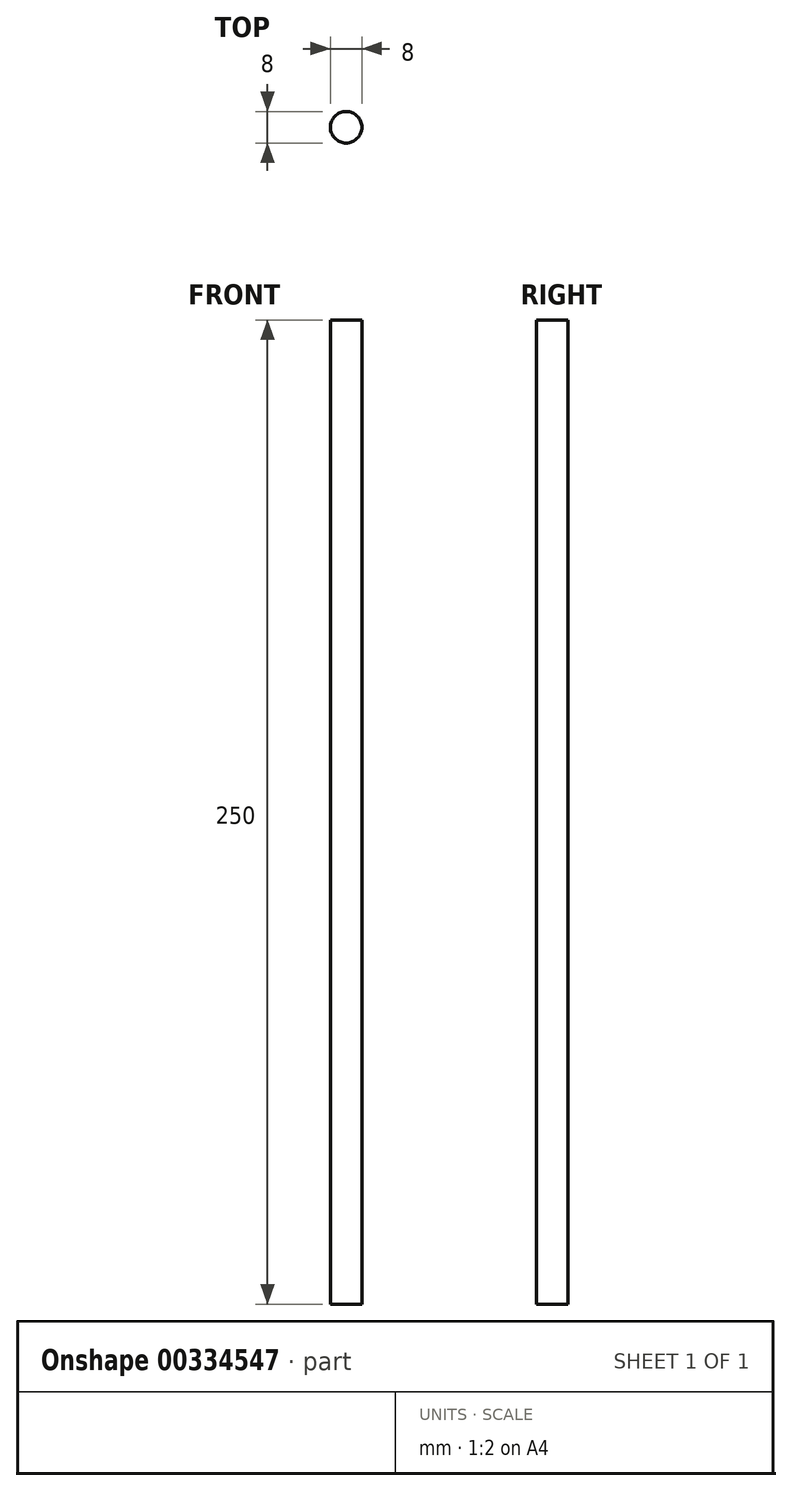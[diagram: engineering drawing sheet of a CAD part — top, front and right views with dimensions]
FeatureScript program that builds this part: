
annotation { "Feature Type Name" : "Feature", "Feature Type Description" : "" }
export const myFeature = defineFeature(function(context is Context, id is Id, definition is map)
    precondition{}
    {
        {
            var Q0;
            Q0=qCreatedBy(makeId("Top.planeOp"),FACE);
            var sketch = newSketch(context, id + "F0", { "sketchPlane" : qUnion([Q0])});
            skCircle(sketch, "E0", {"center": v(0, 0) * mm, "radius": 4 * mm});
            skSolve(sketch);
        }
        {
            var Q0;
            Q0 = qSketchRegion(id + "F0", true);
            extrude(context, id + "F1", {"entities" : qUnion([Q0]), "depth" : 250 * mm});
        }
    });
